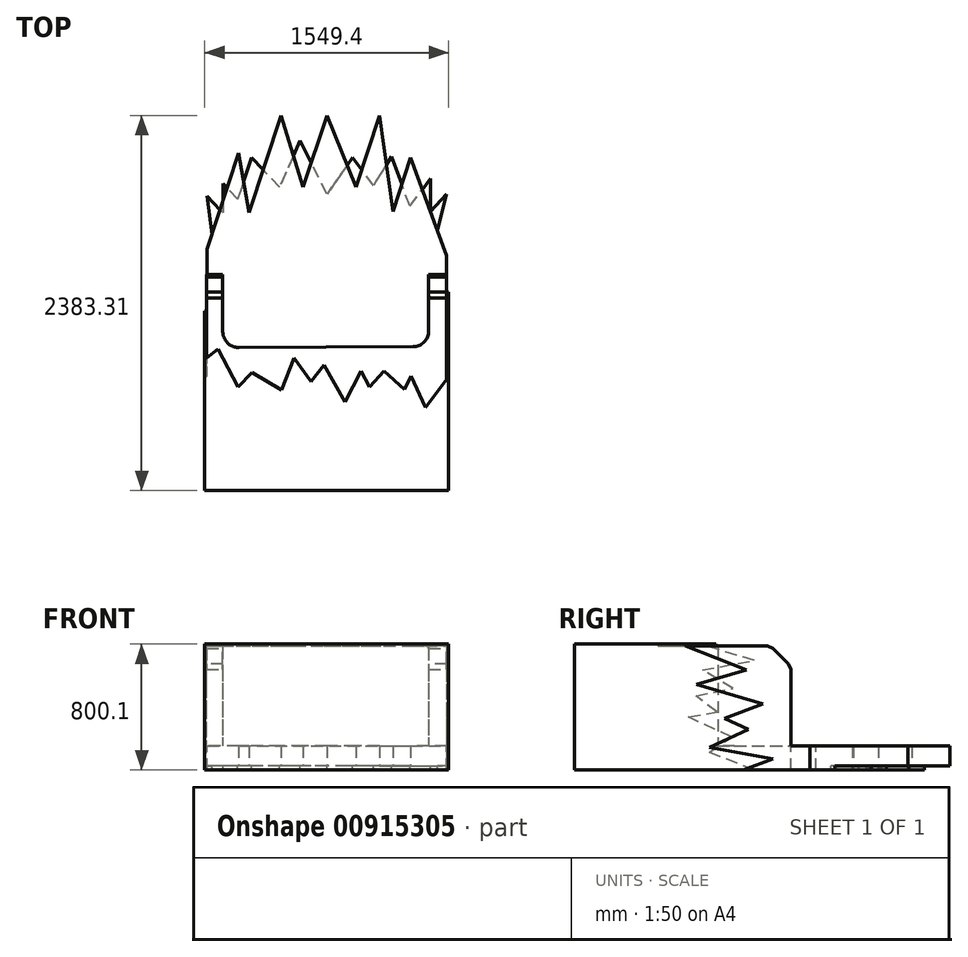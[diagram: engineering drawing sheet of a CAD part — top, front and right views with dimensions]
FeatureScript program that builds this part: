
annotation { "Feature Type Name" : "Feature", "Feature Type Description" : "" }
export const myFeature = defineFeature(function(context is Context, id is Id, definition is map)
    precondition{}
    {
        {
            var Q0;
            Q0=qCreatedBy(makeId("Top.planeOp"),FACE);
            var sketch = newSketch(context, id + "F0", { "sketchPlane" : qUnion([Q0])});
            skLineSegment(sketch, "E0.top", {"start": v(-3498.51, -2613.85) * mm, "end": v(-1974.51, -2613.85) * mm});
            skLineSegment(sketch, "E0.left", {"start": v(-3498.51, -1699.45) * mm, "end": v(-3498.51, -2613.85) * mm});
            skLineSegment(sketch, "E0.right", {"start": v(-1974.51, -1699.45) * mm, "end": v(-1974.51, -2613.85) * mm});
            skLineSegment(sketch, "E1.top", {"start": v(-1974.51, -1240.87) * mm, "end": v(-2088.5, -1240.87) * mm});
            skLineSegment(sketch, "E1.left", {"start": v(-1974.51, -1699.45) * mm, "end": v(-1974.51, -1240.87) * mm});
            skLineSegment(sketch, "E1.right", {"start": v(-2088.5, -1699.45) * mm, "end": v(-2088.5, -1240.87) * mm});
            skLineSegment(sketch, "E2.top", {"start": v(-3498.51, -1240.87) * mm, "end": v(-3396.66, -1240.87) * mm});
            skLineSegment(sketch, "E2.left", {"start": v(-3498.51, -1699.45) * mm, "end": v(-3498.51, -1240.87) * mm});
            skLineSegment(sketch, "E2.right", {"start": v(-3396.66, -1705.04) * mm, "end": v(-3396.66, -1240.87) * mm});
            skLineSegment(sketch, "E3", {"start": v(-3396.66, -1705.04) * mm, "end": v(-2088.5, -1699.45) * mm});
            skSolve(sketch);
        }
        {
            var Q0;
            Q0=makeQuery(id+"F0.imprint","IMPRINT",FACE,{"disambiguationData":[TD([[makeQuery(id+"F0.imprint","IMPRINT",EDGE,{"derivedFrom":sQuery(id+"F0.wireOp",EDGE,"E0.top")}),1.0]])]});
            extrude(context, id + "F1", {"entities" : qUnion([Q0]), "depth" : 762 * mm, "offsetDistance" : 25.4 * mm});
        }
        {
            var Q0;
            Q0=makeQuery(id+"F1.opExtrude","CAP_FACE",FACE,{"disambiguationData":[OSD([sQuery(id+"F0.wireOp",EDGE,"E0.top"),sQuery(id+"F0.wireOp",EDGE,"E0.left"),sQuery(id+"F0.wireOp",EDGE,"E0.right"),sQuery(id+"F0.wireOp",EDGE,"E1.top"),sQuery(id+"F0.wireOp",EDGE,"E1.left"),sQuery(id+"F0.wireOp",EDGE,"E1.right"),sQuery(id+"F0.wireOp",EDGE,"E2.top"),sQuery(id+"F0.wireOp",EDGE,"E2.left"),sQuery(id+"F0.wireOp",EDGE,"E2.right"),sQuery(id+"F0.wireOp",EDGE,"E3")])],"isStart":true});
            var sketch = newSketch(context, id + "F2", { "sketchPlane" : qUnion([Q0])});
            skLineSegment(sketch, "E4.bottom", {"start": v(-1974.51, 2613.85) * mm, "end": v(-3496.48, 2613.85) * mm});
            skLineSegment(sketch, "E4.top", {"start": v(-1974.51, 230.54) * mm, "end": v(-3496.48, 230.54) * mm});
            skLineSegment(sketch, "E4.left", {"start": v(-1974.51, 2613.85) * mm, "end": v(-1974.51, 230.54) * mm});
            skLineSegment(sketch, "E4.right", {"start": v(-3496.48, 2613.85) * mm, "end": v(-3496.48, 230.54) * mm});
            skSolve(sketch);
        }
        {
            var Q0;
            {var subQ1=sQuery(id+"F2.wireOp",EDGE,"E4.top");Q0=makeQuery(id+"F2.imprint","IMPRINT",FACE,{"disambiguationData":[TD([[makeQuery(id+"F2.imprint","IMPRINT",EDGE,{"derivedFrom":subQ1}),-1.0]])]});}
            extrude(context, id + "F3", {"entities" : qUnion([Q0]), "oppositeDirection" : true, "depth" : 127 * mm, "offsetDistance" : 25.4 * mm});
        }
        {
            var Q0;
            Q0=makeQuery(id+"F1.opExtrude","SWEPT_BODY",BODY,{"disambiguationData":[OSD([sQuery(id+"F0.wireOp",EDGE,"E0.top"),sQuery(id+"F0.wireOp",EDGE,"E0.left"),sQuery(id+"F0.wireOp",EDGE,"E0.right"),sQuery(id+"F0.wireOp",EDGE,"E1.top"),sQuery(id+"F0.wireOp",EDGE,"E1.left"),sQuery(id+"F0.wireOp",EDGE,"E1.right"),sQuery(id+"F0.wireOp",EDGE,"E2.top"),sQuery(id+"F0.wireOp",EDGE,"E2.left"),sQuery(id+"F0.wireOp",EDGE,"E2.right"),sQuery(id+"F0.wireOp",EDGE,"E3")])]});
            var Q1;
            Q1=makeQuery(id+"F3.opExtrude","SWEPT_BODY",BODY,{"disambiguationData":[OSD([sQuery(id+"F0.wireOp",EDGE,"E1.top"),sQuery(id+"F0.wireOp",EDGE,"E1.right"),sQuery(id+"F0.wireOp",EDGE,"E2.top"),sQuery(id+"F0.wireOp",EDGE,"E2.right"),sQuery(id+"F0.wireOp",EDGE,"E3"),sQuery(id+"F2.wireOp",EDGE,"E4.top"),sQuery(id+"F2.wireOp",EDGE,"E4.left"),sQuery(id+"F2.wireOp",EDGE,"E4.right")])]});
            booleanBodies(context, id + "F4", {"operationType" : BooleanOperationType.UNION, "tools" : qUnion([Q0, Q1])});
        }
        {
            var Q0;
            {var subQ0=sQuery(id+"F0.wireOp",EDGE,"E3");var subQ1=sQuery(id+"F0.wireOp",EDGE,"E2.right");var subQ2=sQuery(id+"F0.wireOp",EDGE,"E2.top");var subQ3=sQuery(id+"F0.wireOp",EDGE,"E1.right");var subQ4=sQuery(id+"F0.wireOp",EDGE,"E1.top");Q0=makeQuery(id+"F4.opBoolean","MERGE",FACE,{"derivedFrom":[makeQuery(id+"F1.opExtrude","CAP_FACE",FACE,{"disambiguationData":[OSD([sQuery(id+"F0.wireOp",EDGE,"E0.top"),sQuery(id+"F0.wireOp",EDGE,"E0.left"),sQuery(id+"F0.wireOp",EDGE,"E0.right"),subQ4,sQuery(id+"F0.wireOp",EDGE,"E1.left"),subQ3,subQ2,sQuery(id+"F0.wireOp",EDGE,"E2.left"),subQ1,subQ0])],"isStart":true}),makeQuery(id+"F3.opExtrude","CAP_FACE",FACE,{"disambiguationData":[OSD([subQ4,subQ3,subQ2,subQ1,subQ0,sQuery(id+"F2.wireOp",EDGE,"E4.top"),sQuery(id+"F2.wireOp",EDGE,"E4.left"),sQuery(id+"F2.wireOp",EDGE,"E4.right")])],"isStart":true})]});}
            var sketch = newSketch(context, id + "F5", { "sketchPlane" : qUnion([Q0])});
            skLineSegment(sketch, "E5", {"start": v(-2401.69, 230.54) * mm, "end": v(-2551.66, 685.5) * mm});
            skLineSegment(sketch, "E6", {"start": v(-2551.66, 685.5) * mm, "end": v(-2735.5, 230.54) * mm});
            skLineSegment(sketch, "E7", {"start": v(-2735.5, 230.54) * mm, "end": v(-2885.47, 685.5) * mm});
            skLineSegment(sketch, "E8", {"start": v(-2885.47, 685.5) * mm, "end": v(-3027.28, 230.54) * mm});
            skLineSegment(sketch, "E9", {"start": v(-3027.28, 230.54) * mm, "end": v(-3231.06, 848.71) * mm});
            skLineSegment(sketch, "E10", {"start": v(-3231.06, 848.71) * mm, "end": v(-3295.53, 471.22) * mm});
            skLineSegment(sketch, "E11", {"start": v(-3295.53, 471.22) * mm, "end": v(-3496.48, 1080.84) * mm});
            skLineSegment(sketch, "E12", {"start": v(-2401.69, 230.54) * mm, "end": v(-2316.23, 841.82) * mm});
            skLineSegment(sketch, "E13", {"start": v(-2316.23, 841.82) * mm, "end": v(-2203.15, 498.77) * mm});
            skLineSegment(sketch, "E14", {"start": v(-2203.15, 498.77) * mm, "end": v(-1974.51, 1119.29) * mm});
            skSolve(sketch);
        }
        {
            var Q0;
            {var subQ4=sQuery(id+"F5.wireOp",EDGE,"E12");Q0=makeQuery(id+"F5.imprint","IMPRINT",FACE,{"disambiguationData":[TD([[makeQuery(id+"F5.imprint","IMPRINT",EDGE,{"derivedFrom":subQ4}),-1.0]])]});}
            var Q1;
            {var subQ0=sQuery(id+"F5.wireOp",EDGE,"E5");Q1=makeQuery(id+"F5.imprint","IMPRINT",FACE,{"disambiguationData":[TD([[makeQuery(id+"F5.imprint","IMPRINT",EDGE,{"derivedFrom":subQ0}),1.0]])]});}
            var Q2;
            {var subQ4=sQuery(id+"F5.wireOp",EDGE,"E9");Q2=makeQuery(id+"F5.imprint","IMPRINT",FACE,{"disambiguationData":[TD([[makeQuery(id+"F5.imprint","IMPRINT",EDGE,{"derivedFrom":subQ4}),1.0]])]});}
            var Q3;
            {var subQ0=sQuery(id+"F5.wireOp",EDGE,"E7");Q3=makeQuery(id+"F5.imprint","IMPRINT",FACE,{"disambiguationData":[TD([[makeQuery(id+"F5.imprint","IMPRINT",EDGE,{"derivedFrom":subQ0}),1.0]])]});}
            extrude(context, id + "F6", {"entities" : qUnion([Q0, Q1, Q2, Q3]), "operationType" : NewBodyOperationType.REMOVE, "endBound" : BoundingType.THROUGH_ALL, "oppositeDirection" : true, "depth" : 25.4 * mm, "offsetDistance" : 25.4 * mm});
        }
        {
            var Q0;
            {var subQ0=sQuery(id+"F0.wireOp",EDGE,"E3");var subQ1=sQuery(id+"F0.wireOp",EDGE,"E2.right");var subQ2=sQuery(id+"F0.wireOp",EDGE,"E2.top");var subQ3=sQuery(id+"F0.wireOp",EDGE,"E1.right");var subQ4=sQuery(id+"F0.wireOp",EDGE,"E1.top");Q0=makeQuery(id+"F4.opBoolean","MERGE",FACE,{"derivedFrom":[makeQuery(id+"F1.opExtrude","CAP_FACE",FACE,{"disambiguationData":[OSD([sQuery(id+"F0.wireOp",EDGE,"E0.top"),sQuery(id+"F0.wireOp",EDGE,"E0.left"),sQuery(id+"F0.wireOp",EDGE,"E0.right"),subQ4,sQuery(id+"F0.wireOp",EDGE,"E1.left"),subQ3,subQ2,sQuery(id+"F0.wireOp",EDGE,"E2.left"),subQ1,subQ0])],"isStart":true}),makeQuery(id+"F3.opExtrude","CAP_FACE",FACE,{"disambiguationData":[OSD([subQ4,subQ3,subQ2,subQ1,subQ0,sQuery(id+"F2.wireOp",EDGE,"E4.top"),sQuery(id+"F2.wireOp",EDGE,"E4.left"),sQuery(id+"F2.wireOp",EDGE,"E4.right")])],"isStart":true})]});}
            var sketch = newSketch(context, id + "F7", { "sketchPlane" : qUnion([Q0])});
            skLineSegment(sketch, "E15", {"start": v(-2208.74, 806.93) * mm, "end": v(-2325.26, 490.68) * mm});
            skLineSegment(sketch, "E16", {"start": v(-2325.26, 490.68) * mm, "end": v(-2440.9, 676.34) * mm});
            skLineSegment(sketch, "E17", {"start": v(-2440.9, 676.34) * mm, "end": v(-2571.48, 498.77) * mm});
            skLineSegment(sketch, "E18", {"start": v(-2735.5, 729.55) * mm, "end": v(-2905.2, 390.99) * mm});
            skLineSegment(sketch, "E19", {"start": v(-2905.2, 390.99) * mm, "end": v(-3035.8, 685.5) * mm});
            skLineSegment(sketch, "E20", {"start": v(-3035.8, 685.5) * mm, "end": v(-3214.74, 498.77) * mm});
            skLineSegment(sketch, "E21", {"start": v(-3214.74, 498.77) * mm, "end": v(-3301.46, 761.82) * mm});
            skLineSegment(sketch, "E22", {"start": v(-3301.46, 761.82) * mm, "end": v(-3396, 663.15) * mm});
            skPoint(sketch, "E22.endSnap0", {"position": v(-3396, 776.03) * mm});
            skLineSegment(sketch, "E23", {"start": v(-3396, 663.15) * mm, "end": v(-3396, 848.71) * mm});
            skLineSegment(sketch, "E24", {"start": v(-3396, 848.71) * mm, "end": v(-3496.48, 743.86) * mm});
            skLineSegment(sketch, "E25", {"start": v(-3496.48, 743.86) * mm, "end": v(-3465.3, 986.25) * mm});
            skLineSegment(sketch, "E26", {"start": v(-2571.48, 498.77) * mm, "end": v(-2735.5, 729.55) * mm});
            skLineSegment(sketch, "E27", {"start": v(-2208.74, 806.93) * mm, "end": v(-2078.15, 632.82) * mm});
            skLineSegment(sketch, "E28", {"start": v(-2078.15, 632.82) * mm, "end": v(-2078.15, 841.82) * mm});
            skLineSegment(sketch, "E29", {"start": v(-2078.15, 841.82) * mm, "end": v(-1974.51, 729.55) * mm});
            skLineSegment(sketch, "E30", {"start": v(-1974.51, 729.55) * mm, "end": v(-2063.64, 1077.78) * mm});
            skSolve(sketch);
        }
        {
            var Q0;
            {var subQ0=sQuery(id+"F7.wireOp",EDGE,"E19");var subQ1=sQuery(id+"F7.wireOp",EDGE,"E18");var subQ2=makeQuery(id+"F7.imprint","INTERSECT",VERTEX,{"derivedFrom":[subQ1,subQ0]});Q0=makeQuery(id+"F7.imprint","IMPRINT",FACE,{"disambiguationData":[TD([[makeQuery(id+"F7.imprint","IMPRINT",EDGE,{"disambiguationData":[TD([[subQ2,1.0]])],"derivedFrom":subQ1}),-1.0]])]});}
            var Q1;
            {var subQ0=sQuery(id+"F7.wireOp",EDGE,"E21");var subQ1=sQuery(id+"F7.wireOp",EDGE,"E20");var subQ2=makeQuery(id+"F7.imprint","INTERSECT",VERTEX,{"derivedFrom":[subQ1,subQ0]});Q1=makeQuery(id+"F7.imprint","IMPRINT",FACE,{"disambiguationData":[TD([[makeQuery(id+"F7.imprint","IMPRINT",EDGE,{"disambiguationData":[TD([[subQ2,1.0]])],"derivedFrom":subQ1}),-1.0]])]});}
            var Q2;
            {var subQ0=sQuery(id+"F7.wireOp",EDGE,"E25");Q2=makeQuery(id+"F7.imprint","IMPRINT",FACE,{"disambiguationData":[TD([[makeQuery(id+"F7.imprint","IMPRINT",EDGE,{"derivedFrom":subQ0}),-1.0]])]});}
            var Q3;
            {var subQ0=sQuery(id+"F7.wireOp",EDGE,"E23");var subQ1=sQuery(id+"F7.wireOp",EDGE,"E22");var subQ2=makeQuery(id+"F7.imprint","INTERSECT",VERTEX,{"derivedFrom":[subQ1,subQ0]});Q3=makeQuery(id+"F7.imprint","IMPRINT",FACE,{"disambiguationData":[TD([[makeQuery(id+"F7.imprint","IMPRINT",EDGE,{"disambiguationData":[TD([[subQ2,1.0]])],"derivedFrom":subQ1}),-1.0]])]});}
            var Q4;
            {var subQ0=sQuery(id+"F7.wireOp",EDGE,"E26");var subQ1=sQuery(id+"F7.wireOp",EDGE,"E17");var subQ2=makeQuery(id+"F7.imprint","INTERSECT",VERTEX,{"derivedFrom":[subQ1,subQ0]});Q4=makeQuery(id+"F7.imprint","IMPRINT",FACE,{"disambiguationData":[TD([[makeQuery(id+"F7.imprint","IMPRINT",EDGE,{"disambiguationData":[TD([[subQ2,1.0]])],"derivedFrom":subQ1}),-1.0]])]});}
            var Q5;
            {var subQ0=sQuery(id+"F7.wireOp",EDGE,"E16");var subQ1=sQuery(id+"F7.wireOp",EDGE,"E15");var subQ2=makeQuery(id+"F7.imprint","INTERSECT",VERTEX,{"derivedFrom":[subQ1,subQ0]});Q5=makeQuery(id+"F7.imprint","IMPRINT",FACE,{"disambiguationData":[TD([[makeQuery(id+"F7.imprint","IMPRINT",EDGE,{"disambiguationData":[TD([[subQ2,1.0]])],"derivedFrom":subQ1}),-1.0]])]});}
            var Q6;
            {var subQ0=sQuery(id+"F7.wireOp",EDGE,"E28");var subQ1=sQuery(id+"F7.wireOp",EDGE,"E27");var subQ2=makeQuery(id+"F7.imprint","INTERSECT",VERTEX,{"derivedFrom":[subQ1,subQ0]});Q6=makeQuery(id+"F7.imprint","IMPRINT",FACE,{"disambiguationData":[TD([[makeQuery(id+"F7.imprint","IMPRINT",EDGE,{"disambiguationData":[TD([[subQ2,1.0]])],"derivedFrom":subQ1}),1.0]])]});}
            var Q7;
            {var subQ0=sQuery(id+"F7.wireOp",EDGE,"E30");var subQ1=sQuery(id+"F7.wireOp",EDGE,"E29");var subQ2=makeQuery(id+"F7.imprint","INTERSECT",VERTEX,{"derivedFrom":[subQ1,subQ0]});Q7=makeQuery(id+"F7.imprint","IMPRINT",FACE,{"disambiguationData":[TD([[makeQuery(id+"F7.imprint","IMPRINT",EDGE,{"disambiguationData":[TD([[subQ2,1.0]])],"derivedFrom":subQ1}),1.0]])]});}
            var Q8;
            Q8=makeQuery(id+"F7.imprint","IMPRINT",FACE,{"disambiguationData":[TD([[makeQuery(id+"F7.imprint","IMPRINT",EDGE,{"derivedFrom":makeQuery(id+"F1.opExtrude","CAP_EDGE",EDGE,{"disambiguationData":[OSD([sQuery(id+"F0.wireOp",EDGE,"E0.top")])],"isStart":true})}),-1.0]])]});
            extrude(context, id + "F8", {"entities" : qUnion([Q0, Q1, Q2, Q3, Q4, Q5, Q6, Q7, Q8]), "depth" : 25.4 * mm, "offsetDistance" : 25.4 * mm});
        }
        {
            var Q0;
            Q0=makeQuery(id+"F8.opExtrude","SWEPT_BODY",BODY,{"disambiguationData":[OSD([sQuery(id+"F5.wireOp",EDGE,"E14"),sQuery(id+"F7.wireOp",EDGE,"E27"),sQuery(id+"F7.wireOp",EDGE,"E28")])]});
            var Q1;
            Q1=makeQuery(id+"F1.opExtrude","SWEPT_BODY",BODY,{"disambiguationData":[OSD([sQuery(id+"F0.wireOp",EDGE,"E0.top"),sQuery(id+"F0.wireOp",EDGE,"E0.left"),sQuery(id+"F0.wireOp",EDGE,"E0.right"),sQuery(id+"F0.wireOp",EDGE,"E1.top"),sQuery(id+"F0.wireOp",EDGE,"E1.left"),sQuery(id+"F0.wireOp",EDGE,"E1.right"),sQuery(id+"F0.wireOp",EDGE,"E2.top"),sQuery(id+"F0.wireOp",EDGE,"E2.left"),sQuery(id+"F0.wireOp",EDGE,"E2.right"),sQuery(id+"F0.wireOp",EDGE,"E3")])]});
            var Q2;
            Q2=makeQuery(id+"F8.opExtrude","SWEPT_BODY",BODY,{"disambiguationData":[OSD([sQuery(id+"F5.wireOp",EDGE,"E14"),sQuery(id+"F7.wireOp",EDGE,"E29"),sQuery(id+"F7.wireOp",EDGE,"E30")])]});
            var Q3;
            Q3=makeQuery(id+"F8.opExtrude","SWEPT_BODY",BODY,{"disambiguationData":[OSD([sQuery(id+"F5.wireOp",EDGE,"E12"),sQuery(id+"F5.wireOp",EDGE,"E13"),sQuery(id+"F7.wireOp",EDGE,"E15"),sQuery(id+"F7.wireOp",EDGE,"E16")])]});
            var Q4;
            Q4=makeQuery(id+"F8.opExtrude","SWEPT_BODY",BODY,{"disambiguationData":[OSD([sQuery(id+"F5.wireOp",EDGE,"E5"),sQuery(id+"F5.wireOp",EDGE,"E6"),sQuery(id+"F7.wireOp",EDGE,"E17"),sQuery(id+"F7.wireOp",EDGE,"E26")])]});
            var Q5;
            Q5=makeQuery(id+"F8.opExtrude","SWEPT_BODY",BODY,{"disambiguationData":[OSD([sQuery(id+"F5.wireOp",EDGE,"E7"),sQuery(id+"F5.wireOp",EDGE,"E8"),sQuery(id+"F7.wireOp",EDGE,"E18"),sQuery(id+"F7.wireOp",EDGE,"E19")])]});
            var Q6;
            Q6=makeQuery(id+"F8.opExtrude","SWEPT_BODY",BODY,{"disambiguationData":[OSD([sQuery(id+"F5.wireOp",EDGE,"E9"),sQuery(id+"F5.wireOp",EDGE,"E10"),sQuery(id+"F7.wireOp",EDGE,"E20"),sQuery(id+"F7.wireOp",EDGE,"E21")])]});
            var Q7;
            Q7=makeQuery(id+"F8.opExtrude","SWEPT_BODY",BODY,{"disambiguationData":[OSD([sQuery(id+"F5.wireOp",EDGE,"E11"),sQuery(id+"F7.wireOp",EDGE,"E22"),sQuery(id+"F7.wireOp",EDGE,"E23")])]});
            var Q8;
            Q8=makeQuery(id+"F8.opExtrude","SWEPT_BODY",BODY,{"disambiguationData":[OSD([sQuery(id+"F5.wireOp",EDGE,"E11"),sQuery(id+"F7.wireOp",EDGE,"E24"),sQuery(id+"F7.wireOp",EDGE,"E25")])]});
            booleanBodies(context, id + "F9", {"operationType" : BooleanOperationType.UNION, "tools" : qUnion([Q0, Q1, Q2, Q3, Q4, Q5, Q6, Q7, Q8])});
        }
        {
            var Q0;
            Q0=makeQuery(id+"F1.opExtrude","CAP_EDGE",EDGE,{"disambiguationData":[OSD([sQuery(id+"F0.wireOp",EDGE,"E2.top")])],"isStart":false});
            var Q1;
            Q1=makeQuery(id+"F1.opExtrude","CAP_EDGE",EDGE,{"disambiguationData":[OSD([sQuery(id+"F0.wireOp",EDGE,"E1.top")])],"isStart":false});
            chamfer(context, id + "F10", {"entities" : qUnion([Q0, Q1]), "width" : 127 * mm, "tangentPropagation" : true});
        }
        {
            var Q0;
            {var subQ0=sQuery(id+"F0.wireOp",EDGE,"E1.top");Q0=makeQuery(id+"F10.opChamfer","BLEND_EDGE",EDGE,{"blendedFrom":[makeQuery(id+"F1.opExtrude","CAP_EDGE",EDGE,{"disambiguationData":[OSD([subQ0])],"isStart":false}),makeQuery(id+"F1.opExtrude","SWEPT_FACE",FACE,{"disambiguationData":[OSD([subQ0])]})],"blendedInto":[makeQuery(id+"F1.opExtrude","SWEPT_FACE",FACE,{"disambiguationData":[OSD([subQ0])]})]});}
            var Q1;
            {var subQ0=sQuery(id+"F0.wireOp",EDGE,"E1.top");Q1=makeQuery(id+"F10.opChamfer","BLEND_EDGE",EDGE,{"blendedFrom":[makeQuery(id+"F1.opExtrude","CAP_EDGE",EDGE,{"disambiguationData":[OSD([subQ0])],"isStart":false}),makeQuery(id+"F1.opExtrude","CAP_FACE",FACE,{"disambiguationData":[OSD([sQuery(id+"F0.wireOp",EDGE,"E0.top"),sQuery(id+"F0.wireOp",EDGE,"E0.left"),sQuery(id+"F0.wireOp",EDGE,"E0.right"),subQ0,sQuery(id+"F0.wireOp",EDGE,"E1.left"),sQuery(id+"F0.wireOp",EDGE,"E1.right"),sQuery(id+"F0.wireOp",EDGE,"E2.top"),sQuery(id+"F0.wireOp",EDGE,"E2.left"),sQuery(id+"F0.wireOp",EDGE,"E2.right"),sQuery(id+"F0.wireOp",EDGE,"E3")])],"isStart":false})],"blendedInto":[makeQuery(id+"F1.opExtrude","CAP_FACE",FACE,{"disambiguationData":[OSD([sQuery(id+"F0.wireOp",EDGE,"E0.top"),sQuery(id+"F0.wireOp",EDGE,"E0.left"),sQuery(id+"F0.wireOp",EDGE,"E0.right"),subQ0,sQuery(id+"F0.wireOp",EDGE,"E1.left"),sQuery(id+"F0.wireOp",EDGE,"E1.right"),sQuery(id+"F0.wireOp",EDGE,"E2.top"),sQuery(id+"F0.wireOp",EDGE,"E2.left"),sQuery(id+"F0.wireOp",EDGE,"E2.right"),sQuery(id+"F0.wireOp",EDGE,"E3")])],"isStart":false})]});}
            var Q2;
            {var subQ0=sQuery(id+"F0.wireOp",EDGE,"E2.top");Q2=makeQuery(id+"F10.opChamfer","BLEND_EDGE",EDGE,{"blendedFrom":[makeQuery(id+"F1.opExtrude","CAP_EDGE",EDGE,{"disambiguationData":[OSD([subQ0])],"isStart":false}),makeQuery(id+"F9.opBoolean","MERGE",FACE,{"derivedFrom":[makeQuery(id+"F1.opExtrude","SWEPT_FACE",FACE,{"disambiguationData":[OSD([subQ0])]}),makeQuery(id+"F8.opExtrude","SWEPT_FACE",FACE,{"disambiguationData":[OSD([subQ0])]})]})],"blendedInto":[makeQuery(id+"F9.opBoolean","MERGE",FACE,{"derivedFrom":[makeQuery(id+"F1.opExtrude","SWEPT_FACE",FACE,{"disambiguationData":[OSD([subQ0])]}),makeQuery(id+"F8.opExtrude","SWEPT_FACE",FACE,{"disambiguationData":[OSD([subQ0])]})]})]});}
            var Q3;
            {var subQ0=sQuery(id+"F0.wireOp",EDGE,"E2.top");Q3=makeQuery(id+"F10.opChamfer","BLEND_EDGE",EDGE,{"blendedFrom":[makeQuery(id+"F1.opExtrude","CAP_EDGE",EDGE,{"disambiguationData":[OSD([subQ0])],"isStart":false}),makeQuery(id+"F1.opExtrude","CAP_FACE",FACE,{"disambiguationData":[OSD([sQuery(id+"F0.wireOp",EDGE,"E0.top"),sQuery(id+"F0.wireOp",EDGE,"E0.left"),sQuery(id+"F0.wireOp",EDGE,"E0.right"),sQuery(id+"F0.wireOp",EDGE,"E1.top"),sQuery(id+"F0.wireOp",EDGE,"E1.left"),sQuery(id+"F0.wireOp",EDGE,"E1.right"),subQ0,sQuery(id+"F0.wireOp",EDGE,"E2.left"),sQuery(id+"F0.wireOp",EDGE,"E2.right"),sQuery(id+"F0.wireOp",EDGE,"E3")])],"isStart":false})],"blendedInto":[makeQuery(id+"F1.opExtrude","CAP_FACE",FACE,{"disambiguationData":[OSD([sQuery(id+"F0.wireOp",EDGE,"E0.top"),sQuery(id+"F0.wireOp",EDGE,"E0.left"),sQuery(id+"F0.wireOp",EDGE,"E0.right"),sQuery(id+"F0.wireOp",EDGE,"E1.top"),sQuery(id+"F0.wireOp",EDGE,"E1.left"),sQuery(id+"F0.wireOp",EDGE,"E1.right"),subQ0,sQuery(id+"F0.wireOp",EDGE,"E2.left"),sQuery(id+"F0.wireOp",EDGE,"E2.right"),sQuery(id+"F0.wireOp",EDGE,"E3")])],"isStart":false})]});}
            chamfer(context, id + "F11", {"entities" : qUnion([Q0, Q1, Q2, Q3]), "width" : 50.8 * mm, "tangentPropagation" : true});
        }
        {
            var Q0;
            Q0=makeQuery(id+"F1.opExtrude","SWEPT_EDGE",EDGE,{"disambiguationData":[OSD([sQuery(id+"F0.wireOp",EDGE,"E2.right"),sQuery(id+"F0.wireOp",EDGE,"E3")])]});
            var Q1;
            Q1=makeQuery(id+"F1.opExtrude","SWEPT_EDGE",EDGE,{"disambiguationData":[OSD([sQuery(id+"F0.wireOp",EDGE,"E1.right"),sQuery(id+"F0.wireOp",EDGE,"E3")])]});
            fillet(context, id + "F12", {"entities" : qUnion([Q0, Q1]), "radius" : 101.6 * mm, "tangentPropagation" : true, "allowEdgeOverflow" : false});
        }
        {
            var Q0;
            Q0=makeQuery(id+"F1.opExtrude","CAP_EDGE",EDGE,{"disambiguationData":[OSD([sQuery(id+"F0.wireOp",EDGE,"E3")])],"isStart":false});
            fillet(context, id + "F13", {"entities" : qUnion([Q0]), "radius" : 5.08 * mm, "tangentPropagation" : true, "allowEdgeOverflow" : false});
        }
        {
            var Q0;
            {var subQ0=sQuery(id+"F2.wireOp",EDGE,"E4.left");var subQ1=sQuery(id+"F0.wireOp",EDGE,"E1.left");var subQ2=sQuery(id+"F0.wireOp",EDGE,"E0.right");Q0=makeQuery(id+"F9.opBoolean","MERGE",FACE,{"derivedFrom":[makeQuery(id+"F4.opBoolean","MERGE",FACE,{"derivedFrom":[makeQuery(id+"F1.opExtrude","SWEPT_FACE",FACE,{"disambiguationData":[OSD([subQ2,subQ1])]}),makeQuery(id+"F3.opExtrude","SWEPT_FACE",FACE,{"disambiguationData":[OSD([subQ0])]})]}),makeQuery(id+"F8.opExtrude","SWEPT_FACE",FACE,{"disambiguationData":[OSD([subQ2,subQ1,subQ0])]})]});}
            var sketch = newSketch(context, id + "F14", { "sketchPlane" : qUnion([Q0])});
            skLineSegment(sketch, "E31", {"start": v(-1908.93, 762) * mm, "end": v(-1524, 610.36) * mm});
            skLineSegment(sketch, "E32", {"start": v(-1524, 610.36) * mm, "end": v(-1839.84, 518.24) * mm});
            skLineSegment(sketch, "E33", {"start": v(-1839.84, 518.24) * mm, "end": v(-1418.67, 396.51) * mm});
            skLineSegment(sketch, "E34", {"start": v(-1418.67, 396.51) * mm, "end": v(-1662.18, 304.4) * mm});
            skLineSegment(sketch, "E35", {"start": v(-1662.18, 304.4) * mm, "end": v(-1510.85, 232.01) * mm});
            skLineSegment(sketch, "E36", {"start": v(-1510.85, 232.01) * mm, "end": v(-1757.6, 120.15) * mm});
            skLineSegment(sketch, "E37", {"start": v(-1757.6, 120.15) * mm, "end": v(-1352.93, 44.49) * mm});
            skLineSegment(sketch, "E38", {"start": v(-1352.93, 44.49) * mm, "end": v(-1540.45, -25.4) * mm});
            skSolve(sketch);
        }
        {
            var Q0;
            {var subQ7=sQuery(id+"F14.wireOp",EDGE,"E31");Q0=makeQuery(id+"F14.imprint","IMPRINT",FACE,{"disambiguationData":[TD([[makeQuery(id+"F14.imprint","IMPRINT",EDGE,{"derivedFrom":subQ7}),-1.0]])]});}
            extrude(context, id + "F15", {"entities" : qUnion([Q0]), "operationType" : NewBodyOperationType.ADD, "depth" : 12.7 * mm, "offsetDistance" : 25.4 * mm});
        }
        {
            var Q0;
            {var subQ0=sQuery(id+"F0.wireOp",EDGE,"E2.left");var subQ1=sQuery(id+"F0.wireOp",EDGE,"E0.left");Q0=makeQuery(id+"F9.opBoolean","MERGE",FACE,{"derivedFrom":[makeQuery(id+"F1.opExtrude","SWEPT_FACE",FACE,{"disambiguationData":[OSD([subQ1,subQ0])]}),makeQuery(id+"F8.opExtrude","SWEPT_FACE",FACE,{"disambiguationData":[OSD([subQ1,subQ0])]})]});}
            var sketch = newSketch(context, id + "F16", { "sketchPlane" : qUnion([Q0])});
            skLineSegment(sketch, "E39", {"start": v(1473.07, -25.4) * mm, "end": v(1758.89, 87.98) * mm});
            skLineSegment(sketch, "E40", {"start": v(1758.89, 87.98) * mm, "end": v(1617.7, 184.4) * mm});
            skLineSegment(sketch, "E41", {"start": v(1617.7, 184.4) * mm, "end": v(1889.74, 311.81) * mm});
            skLineSegment(sketch, "E42", {"start": v(1889.74, 311.81) * mm, "end": v(1710.68, 342.8) * mm});
            skLineSegment(sketch, "E43", {"start": v(1710.68, 342.8) * mm, "end": v(1844.98, 446.11) * mm});
            skLineSegment(sketch, "E44", {"start": v(1844.98, 446.11) * mm, "end": v(1607.37, 494.32) * mm});
            skLineSegment(sketch, "E45", {"start": v(1607.37, 494.32) * mm, "end": v(1803.66, 611.4) * mm});
            skLineSegment(sketch, "E46", {"start": v(1803.66, 611.4) * mm, "end": v(1473.07, 669.94) * mm});
            skLineSegment(sketch, "E47", {"start": v(1473.07, 669.94) * mm, "end": v(1772.66, 762) * mm});
            skSolve(sketch);
        }
        {
            var Q0;
            {var subQ5=sQuery(id+"F16.wireOp",EDGE,"E39");Q0=makeQuery(id+"F16.imprint","IMPRINT",FACE,{"disambiguationData":[TD([[makeQuery(id+"F16.imprint","IMPRINT",EDGE,{"derivedFrom":subQ5}),-1.0]])]});}
            extrude(context, id + "F17", {"entities" : qUnion([Q0]), "operationType" : NewBodyOperationType.ADD, "depth" : 12.7 * mm, "offsetDistance" : 25.4 * mm});
        }
        {
            var Q0;
            {var subQ0=sQuery(id+"F0.wireOp",EDGE,"E2.left");var subQ1=sQuery(id+"F0.wireOp",EDGE,"E0.left");var subQ2=makeQuery(id+"F1.opExtrude","CAP_EDGE",EDGE,{"disambiguationData":[OSD([subQ1,subQ0])],"isStart":false});var subQ3=sQuery(id+"F0.wireOp",EDGE,"E0.top");var subQ4=sQuery(id+"F0.wireOp",EDGE,"E1.left");var subQ5=sQuery(id+"F0.wireOp",EDGE,"E0.right");Q0=makeQuery(id+"F17.boolean.opBoolean","MERGE",FACE,{"derivedFrom":[makeQuery(id+"F15.boolean.opBoolean","MERGE",FACE,{"derivedFrom":[makeQuery(id+"F1.opExtrude","CAP_FACE",FACE,{"disambiguationData":[OSD([subQ3,subQ1,subQ5,sQuery(id+"F0.wireOp",EDGE,"E1.top"),subQ4,sQuery(id+"F0.wireOp",EDGE,"E1.right"),sQuery(id+"F0.wireOp",EDGE,"E2.top"),subQ0,sQuery(id+"F0.wireOp",EDGE,"E2.right"),sQuery(id+"F0.wireOp",EDGE,"E3")])],"isStart":false}),makeQuery(id+"F15.opExtrude","SWEPT_FACE",FACE,{"disambiguationData":[OSD([subQ5,subQ4])]})]}),makeQuery(id+"F17.opExtrude","SWEPT_FACE",FACE,{"disambiguationData":[OSD([subQ1,subQ0]),TDD([makeQuery(id+"F16.imprint","IMPRINT",EDGE,{"disambiguationData":[TD([[makeQuery(id+"F16.imprint","INTERSECT",VERTEX,{"derivedFrom":[subQ2,sQuery(id+"F16.wireOp",EDGE,"E47")]}),1.0]])],"derivedFrom":subQ2})])]})]});}
            var sketch = newSketch(context, id + "F18", { "sketchPlane" : qUnion([Q0])});
            skLineSegment(sketch, "E48", {"start": v(-3498.51, -1772.66) * mm, "end": v(-3426.7, -1715.43) * mm});
            skLineSegment(sketch, "E49", {"start": v(-3426.7, -1715.43) * mm, "end": v(-3299.12, -1954.3) * mm});
            skLineSegment(sketch, "E50", {"start": v(-3299.12, -1954.3) * mm, "end": v(-3209.55, -1862) * mm});
            skLineSegment(sketch, "E51", {"start": v(-3209.55, -1862) * mm, "end": v(-3024.97, -1976.01) * mm});
            skLineSegment(sketch, "E52", {"start": v(-3024.97, -1976.01) * mm, "end": v(-2943.53, -1772.66) * mm});
            skLineSegment(sketch, "E53", {"start": v(-2943.53, -1772.66) * mm, "end": v(-2837.67, -1921.72) * mm});
            skLineSegment(sketch, "E54", {"start": v(-2837.67, -1921.72) * mm, "end": v(-2753.52, -1815.86) * mm});
            skLineSegment(sketch, "E55", {"start": v(-2753.52, -1815.86) * mm, "end": v(-2620.52, -2052.02) * mm});
            skLineSegment(sketch, "E56", {"start": v(-2620.52, -2052.02) * mm, "end": v(-2517.37, -1853.86) * mm});
            skLineSegment(sketch, "E57", {"start": v(-2517.37, -1853.86) * mm, "end": v(-2465.8, -1957.01) * mm});
            skLineSegment(sketch, "E58", {"start": v(-2465.8, -1957.01) * mm, "end": v(-2373.5, -1853.86) * mm});
            skLineSegment(sketch, "E59", {"start": v(-2373.5, -1853.86) * mm, "end": v(-2242.43, -1971.14) * mm});
            skLineSegment(sketch, "E60", {"start": v(-2242.43, -1971.14) * mm, "end": v(-2202.5, -1886.44) * mm});
            skLineSegment(sketch, "E61", {"start": v(-2202.5, -1886.44) * mm, "end": v(-2110.2, -2084.6) * mm});
            skLineSegment(sketch, "E62", {"start": v(-2110.2, -2084.6) * mm, "end": v(-1974.51, -1908.93) * mm});
            skSolve(sketch);
        }
        {
            var Q0;
            Q0=makeQuery(id+"F18.imprint","IMPRINT",FACE,{"disambiguationData":[TD([[makeQuery(id+"F18.imprint","IMPRINT",EDGE,{"derivedFrom":sQuery(id+"F18.wireOp",EDGE,"E48")}),-1.0]])]});
            extrude(context, id + "F19", {"entities" : qUnion([Q0]), "operationType" : NewBodyOperationType.ADD, "depth" : 12.7 * mm, "offsetDistance" : 25.4 * mm});
        }
    });
